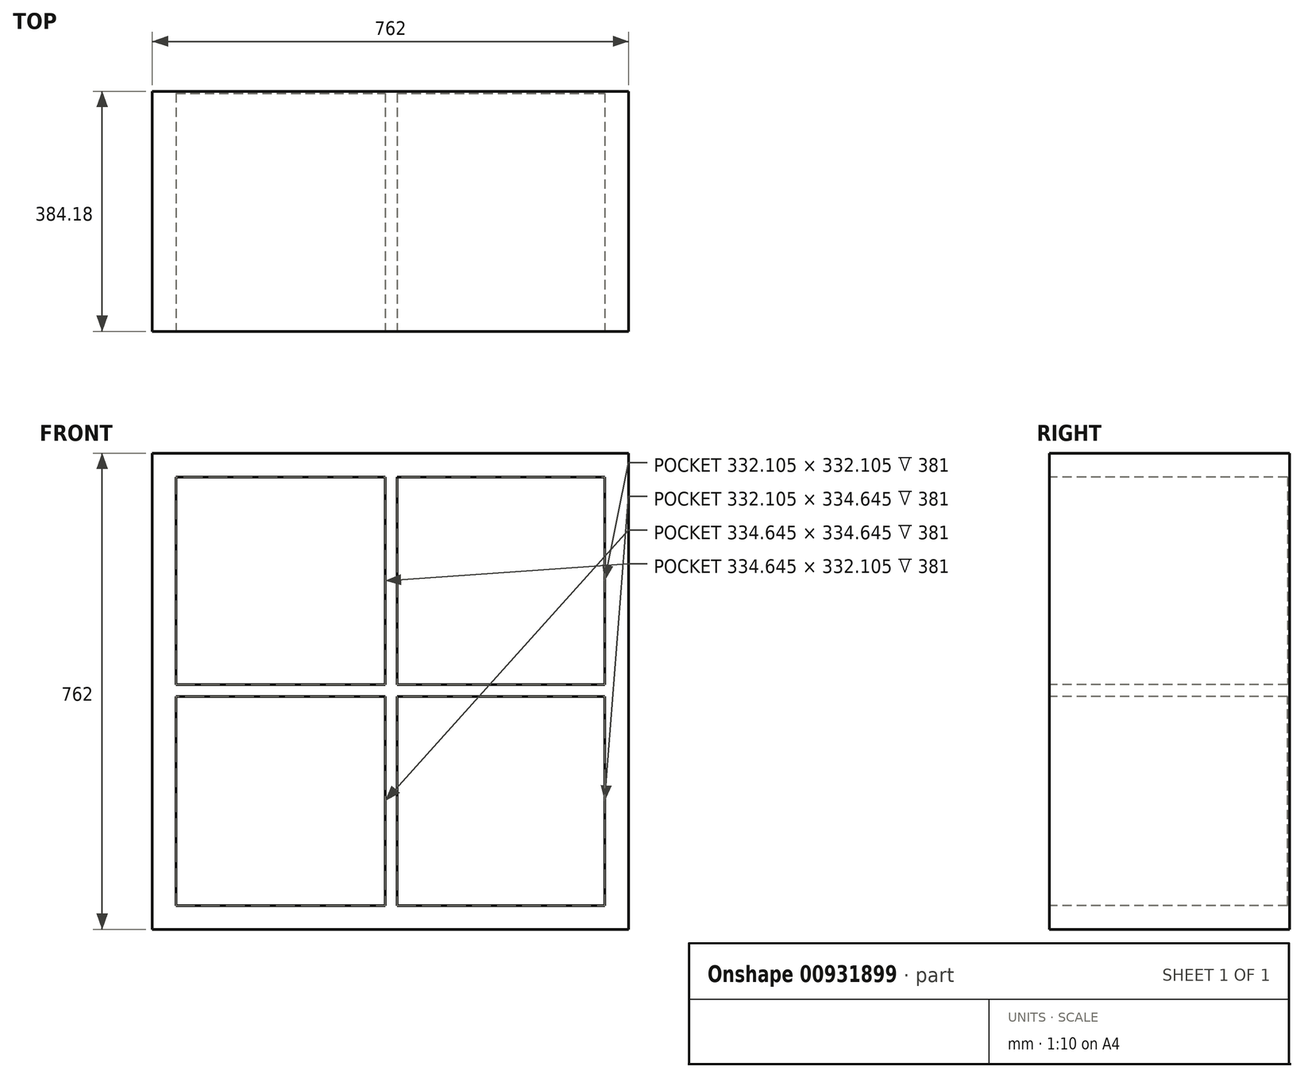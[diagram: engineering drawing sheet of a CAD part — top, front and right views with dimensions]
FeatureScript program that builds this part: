
annotation { "Feature Type Name" : "Feature", "Feature Type Description" : "" }
export const myFeature = defineFeature(function(context is Context, id is Id, definition is map)
    precondition{}
    {
        {
            var Q0;
            Q0=qCreatedBy(makeId("Front.planeOp"),FACE);
            var sketch = newSketch(context, id + "F0", { "sketchPlane" : qUnion([Q0])});
            skLineSegment(sketch, "E0.bottom", {"start": v(0, 0) * mm, "end": v(762, 0) * mm});
            skLineSegment(sketch, "E0.top", {"start": v(0, -762) * mm, "end": v(762, -762) * mm});
            skLineSegment(sketch, "E0.left", {"start": v(0, 0) * mm, "end": v(0, -762) * mm});
            skLineSegment(sketch, "E0.right", {"start": v(762, 0) * mm, "end": v(762, -762) * mm});
            skLineSegment(sketch, "E1.0", {"start": v(38.1, -38.1) * mm, "end": v(372.75, -38.1) * mm});
            skLineSegment(sketch, "E1.1", {"start": v(38.1, -38.1) * mm, "end": v(38.1, -370.2) * mm});
            skLineSegment(sketch, "E1.2", {"start": v(38.1, -723.9) * mm, "end": v(372.75, -723.9) * mm});
            skLineSegment(sketch, "E1.3", {"start": v(723.9, -38.1) * mm, "end": v(723.9, -370.2) * mm});
            skLineSegment(sketch, "E2", {"start": v(372.75, -38.1) * mm, "end": v(372.75, -370.2) * mm});
            skLineSegment(sketch, "E3", {"start": v(372.75, -370.2) * mm, "end": v(38.1, -370.2) * mm});
            skLineSegment(sketch, "E4", {"start": v(38.1, -389.26) * mm, "end": v(372.75, -389.25) * mm});
            skLineSegment(sketch, "E5", {"start": v(372.75, -389.25) * mm, "end": v(372.75, -723.9) * mm});
            skLineSegment(sketch, "E6", {"start": v(391.8, -38.1) * mm, "end": v(391.8, -370.2) * mm});
            skLineSegment(sketch, "E7", {"start": v(391.8, -370.2) * mm, "end": v(723.9, -370.2) * mm});
            skLineSegment(sketch, "E8", {"start": v(391.8, -723.9) * mm, "end": v(391.8, -389.25) * mm});
            skLineSegment(sketch, "E9", {"start": v(391.8, -389.25) * mm, "end": v(723.9, -389.25) * mm});
            skLineSegment(sketch, "E10.trimOffspring", {"start": v(38.1, -389.26) * mm, "end": v(38.1, -723.9) * mm});
            skLineSegment(sketch, "E11.trimOffspring", {"start": v(391.8, -38.1) * mm, "end": v(723.9, -38.1) * mm});
            skLineSegment(sketch, "E12.trimOffspring", {"start": v(723.9, -389.25) * mm, "end": v(723.9, -723.9) * mm});
            skLineSegment(sketch, "E13.trimOffspring", {"start": v(391.8, -723.9) * mm, "end": v(723.9, -723.9) * mm});
            skSolve(sketch);
        }
        {
            var Q0;
            Q0 = qSketchRegion(id + "F0", true);
            extrude(context, id + "F1", {"entities" : qUnion([Q0]), "oppositeDirection" : true, "depth" : 381 * mm, "offsetDistance" : 25.4 * mm});
        }
        {
            var Q0;
            Q0=makeQuery(id+"F1.opExtrude","CAP_FACE",FACE,{"disambiguationData":[OSD([sQuery(id+"F0.wireOp",EDGE,"E0.bottom"),sQuery(id+"F0.wireOp",EDGE,"E0.top"),sQuery(id+"F0.wireOp",EDGE,"E0.left"),sQuery(id+"F0.wireOp",EDGE,"E0.right"),sQuery(id+"F0.wireOp",EDGE,"E1.0"),sQuery(id+"F0.wireOp",EDGE,"E1.1"),sQuery(id+"F0.wireOp",EDGE,"E1.2"),sQuery(id+"F0.wireOp",EDGE,"E1.3"),sQuery(id+"F0.wireOp",EDGE,"E2"),sQuery(id+"F0.wireOp",EDGE,"E3"),sQuery(id+"F0.wireOp",EDGE,"E4"),sQuery(id+"F0.wireOp",EDGE,"E5"),sQuery(id+"F0.wireOp",EDGE,"E6"),sQuery(id+"F0.wireOp",EDGE,"E7"),sQuery(id+"F0.wireOp",EDGE,"E8"),sQuery(id+"F0.wireOp",EDGE,"E9"),sQuery(id+"F0.wireOp",EDGE,"E10.trimOffspring"),sQuery(id+"F0.wireOp",EDGE,"E11.trimOffspring"),sQuery(id+"F0.wireOp",EDGE,"E12.trimOffspring"),sQuery(id+"F0.wireOp",EDGE,"E13.trimOffspring")])],"isStart":false});
            var sketch = newSketch(context, id + "F2", { "sketchPlane" : qUnion([Q0])});
            skLineSegment(sketch, "E14.bottom", {"start": v(-762, 0) * mm, "end": v(0, 0) * mm});
            skLineSegment(sketch, "E14.top", {"start": v(-762, -762) * mm, "end": v(0, -762) * mm});
            skLineSegment(sketch, "E14.left", {"start": v(-762, 0) * mm, "end": v(-762, -762) * mm});
            skLineSegment(sketch, "E14.right", {"start": v(0, 0) * mm, "end": v(0, -762) * mm});
            skSolve(sketch);
        }
        {
            var Q0;
            Q0 = qSketchRegion(id + "F2", true);
            extrude(context, id + "F3", {"entities" : qUnion([Q0]), "operationType" : NewBodyOperationType.ADD, "depth" : 3.17 * mm, "offsetDistance" : 25.4 * mm});
        }
    });
